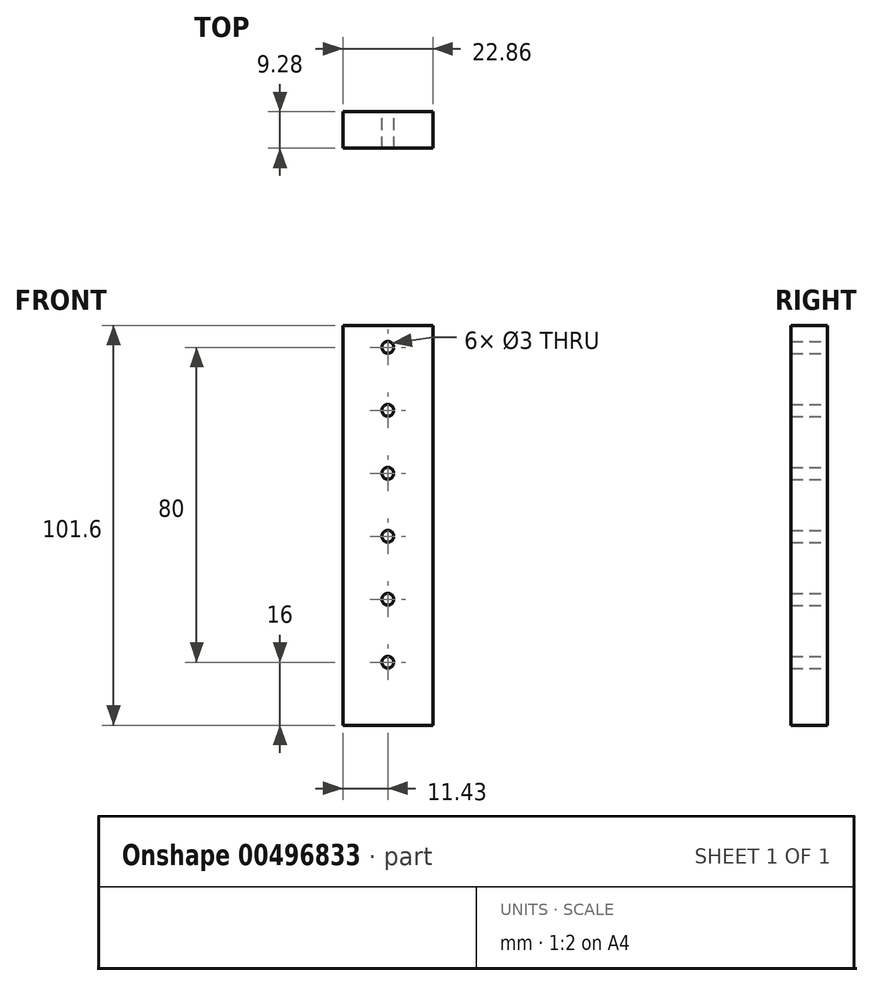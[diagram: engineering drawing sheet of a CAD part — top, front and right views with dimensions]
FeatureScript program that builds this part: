
annotation { "Feature Type Name" : "Feature", "Feature Type Description" : "" }
export const myFeature = defineFeature(function(context is Context, id is Id, definition is map)
    precondition{}
    {
        {
            var Q0;
            Q0=qCreatedBy(makeId("Top.planeOp"),FACE);
            var sketch = newSketch(context, id + "F0", { "sketchPlane" : qUnion([Q0])});
            skLineSegment(sketch, "E0.bottom", {"start": v(-11.43, 4.64) * mm, "end": v(11.43, 4.64) * mm});
            skLineSegment(sketch, "E0.top", {"start": v(-11.43, -4.64) * mm, "end": v(11.43, -4.64) * mm});
            skLineSegment(sketch, "E0.left", {"start": v(-11.43, 4.64) * mm, "end": v(-11.43, -4.64) * mm});
            skLineSegment(sketch, "E0.right", {"start": v(11.43, 4.64) * mm, "end": v(11.43, -4.64) * mm});
            skPoint(sketch, "E0.middle", {"position": v(0, 0) * mm});
            skSolve(sketch);
        }
        {
            var Q0;
            Q0=makeQuery(id+"F0.imprint","IMPRINT",FACE,{"disambiguationData":[TD([[makeQuery(id+"F0.imprint","IMPRINT",EDGE,{"derivedFrom":sQuery(id+"F0.wireOp",EDGE,"E0.bottom")}),-1.0]])]});
            extrude(context, id + "F1", {"entities" : qUnion([Q0]), "depth" : 101.6 * mm});
        }
        {
            var Q0;
            Q0=makeQuery(id+"F1.opExtrude","SWEPT_FACE",FACE,{"disambiguationData":[OSD([sQuery(id+"F0.wireOp",EDGE,"E0.bottom")])]});
            var sketch = newSketch(context, id + "F2", { "sketchPlane" : qUnion([Q0])});
            skLineSegment(sketch, "E1", {"start": v(0, 0) * mm, "end": v(0, 101.6) * mm});
            skCircle(sketch, "E2", {"center": v(0, 16) * mm, "radius": 1.5 * mm});
            skCircle(sketch, "E3.0.1.0", {"center": v(0, 32) * mm, "radius": 1.5 * mm});
            skCircle(sketch, "E3.0.2.0", {"center": v(0, 48) * mm, "radius": 1.5 * mm});
            skCircle(sketch, "E3.0.3.0", {"center": v(0, 64) * mm, "radius": 1.5 * mm});
            skLineSegment(sketch, "E3.direction1", {"start": v(0, 16) * mm, "end": v(25.4, 16) * mm, "construction": true});
            skLineSegment(sketch, "E3.direction2", {"start": v(0, 16) * mm, "end": v(0, 32) * mm, "construction": true});
            skCircle(sketch, "E4.0.0.4", {"center": v(0, 80) * mm, "radius": 1.5 * mm});
            skCircle(sketch, "E4.0.0.5", {"center": v(0, 96) * mm, "radius": 1.5 * mm});
            skCircle(sketch, "E4.0.0.6", {"center": v(0, 112) * mm, "radius": 1.5 * mm});
            skSolve(sketch);
        }
        {
            var Q0;
            Q0 = qSketchRegion(id + "F2", true);
            extrude(context, id + "F3", {"entities" : qUnion([Q0]), "operationType" : NewBodyOperationType.REMOVE, "oppositeDirection" : true, "depth" : 25.4 * mm});
        }
    });
